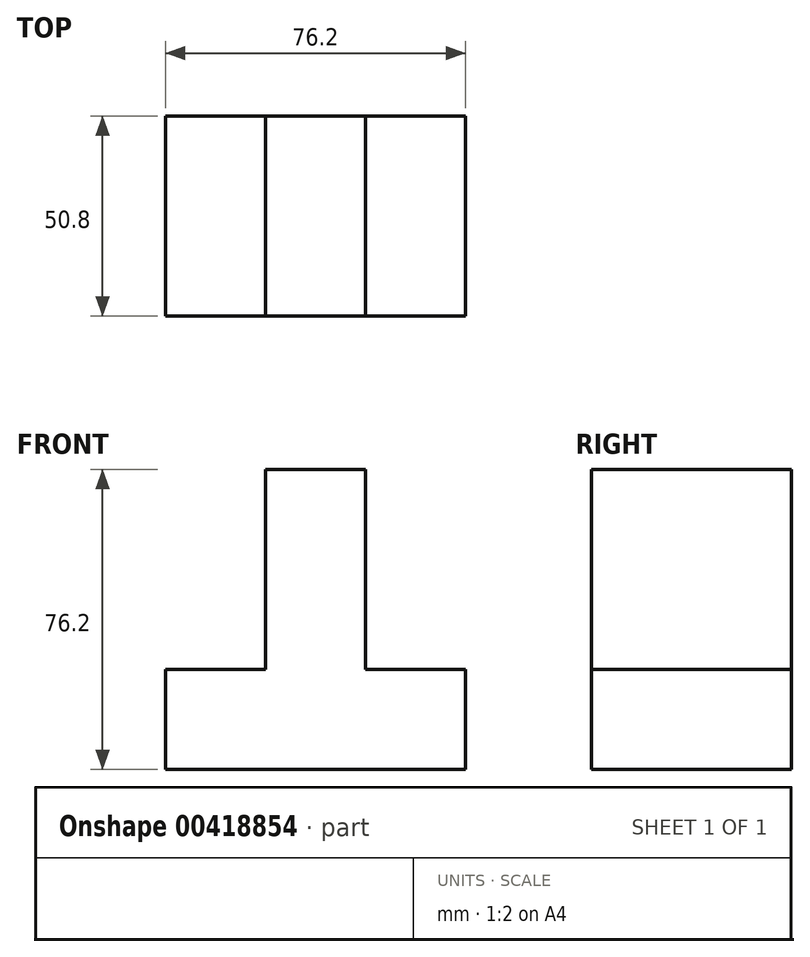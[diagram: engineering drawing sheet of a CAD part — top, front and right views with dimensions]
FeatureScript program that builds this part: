
annotation { "Feature Type Name" : "Feature", "Feature Type Description" : "" }
export const myFeature = defineFeature(function(context is Context, id is Id, definition is map)
    precondition{}
    {
        {
            var Q0;
            Q0=qCreatedBy(makeId("Front.planeOp"),FACE);
            var sketch = newSketch(context, id + "F0", { "sketchPlane" : qUnion([Q0])});
            skLineSegment(sketch, "E0", {"start": v(0, 0) * mm, "end": v(-76.2, 0) * mm});
            skLineSegment(sketch, "E1", {"start": v(-76.2, 0) * mm, "end": v(-76.2, 25.4) * mm});
            skLineSegment(sketch, "E2", {"start": v(-76.2, 25.4) * mm, "end": v(-50.8, 25.4) * mm});
            skLineSegment(sketch, "E3", {"start": v(-50.8, 25.4) * mm, "end": v(-50.8, 76.2) * mm});
            skLineSegment(sketch, "E4", {"start": v(0, 0) * mm, "end": v(0, 25.4) * mm});
            skLineSegment(sketch, "E5", {"start": v(0, 25.4) * mm, "end": v(-25.4, 25.4) * mm});
            skLineSegment(sketch, "E6", {"start": v(-25.4, 25.4) * mm, "end": v(-25.4, 76.2) * mm});
            skLineSegment(sketch, "E7", {"start": v(-25.4, 76.2) * mm, "end": v(-50.8, 76.2) * mm});
            skSolve(sketch);
        }
        {
            var Q0;
            Q0 = qSketchRegion(id + "F0", true);
            extrude(context, id + "F1", {"entities" : qUnion([Q0]), "depth" : 50.8 * mm});
        }
    });
